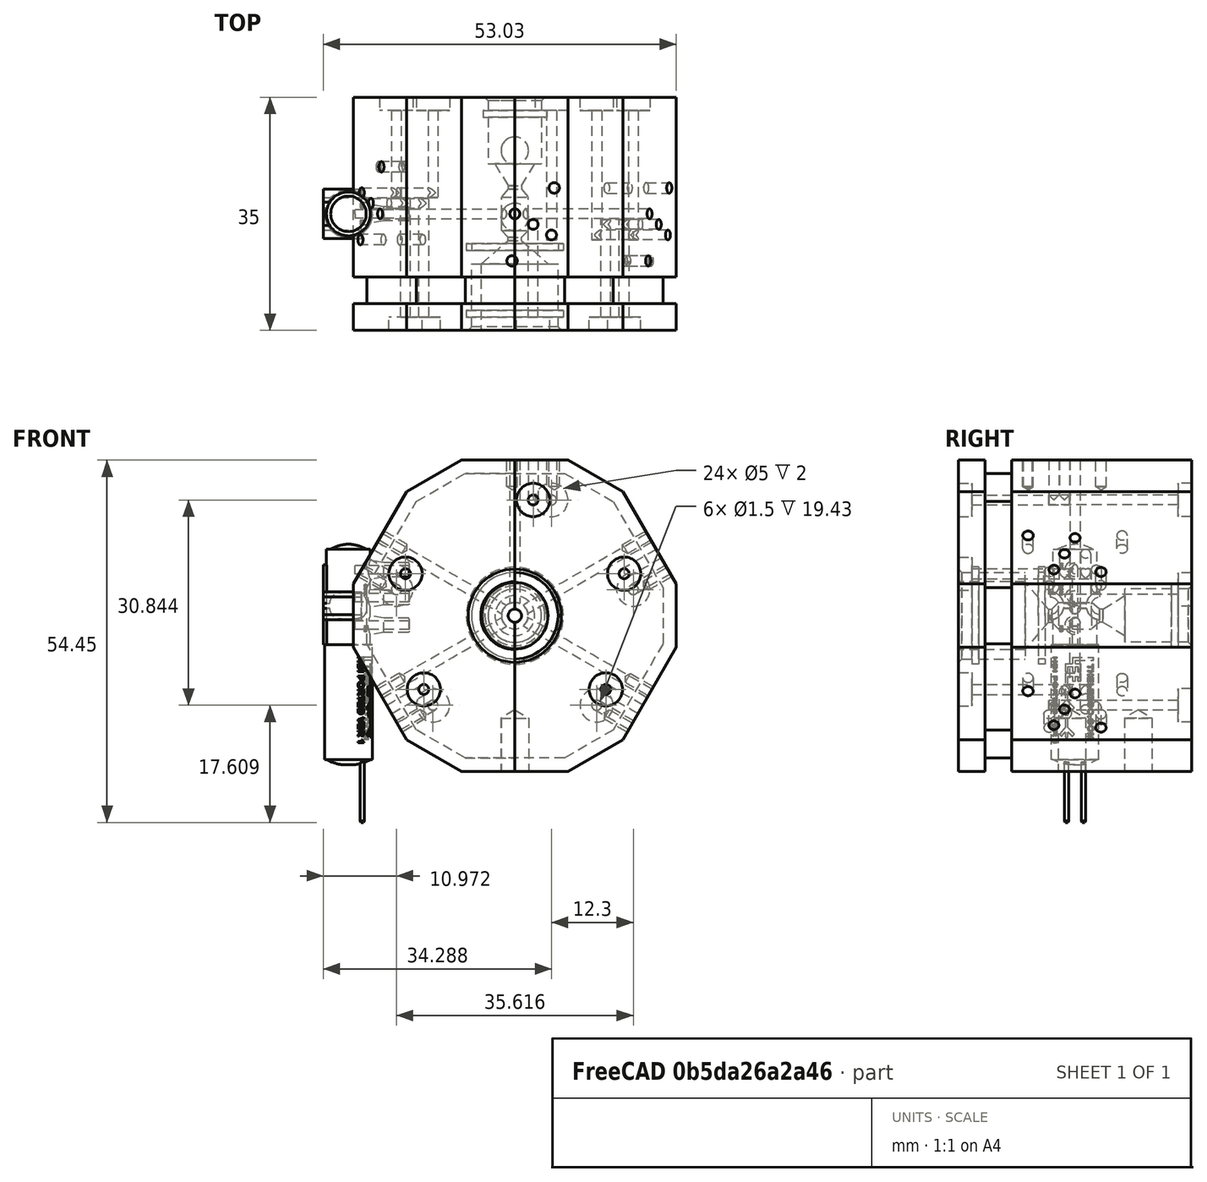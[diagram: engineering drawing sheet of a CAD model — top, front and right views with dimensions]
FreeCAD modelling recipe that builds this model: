
FCSTD DOCUMENT  (FreeCAD 0.18.4R)
Label: main_halved_for_measurements
Comment: # 2020-08-05 14:49:47: read from <userpath>/repositories/sussex_neuro/Olfactometer/hardware/mechanics/from_raiser_et_al/nozzle_big.ipt
License: All rights reserved
LicenseURL: http://en.wikipedia.org/wiki/All_rights_reserved
objects: App::MeasureDistance×10, Part::Feature×6, Part::Cylinder×6, Part::Cut×5, Part::MultiFuse×3, App::FeaturePython×2, Part::Box×2, Part::Fuse×1, PartDesign::FeatureBase×1, PartDesign::Body×1
note: 25 computed .brp shape members not serialized (recipe doc carries the construction recipe); baked Part::Feature solids carry a one-line shape summary decoded from their .brp

FEATURE [Part::Feature] Part__Feature  label="main"
  shape: bbox 48.5 x 35 x 46.77 mm, 148 faces, 0 solids (baked)
FEATURE [Part::Feature] Part__Feature002  label="nozzle_small"
  Placement = pos=(0,2.5,0) rot=(-1,0,0;1.5708rad)
  shape: bbox 8 x 5 x 8 mm, 6 faces (baked)
FEATURE [Part::Feature] Part__Feature004  label="nozzle_big"
  Placement = pos=(0,-2.5,0) rot=(1,0,0;1.5708rad)
  shape: bbox 13 x 5 x 13 mm, 6 faces (baked)
FEATURE [Part::Feature] Part__Feature_solid  label="main (Solid)"
  shape: bbox 48.5 x 35 x 46.77 mm, 148 faces (baked)
FEATURE [Part::MultiFuse] Fusion  label="boddy_fusion_nozzles"
  Shapes = -> [Part__Feature002,Part__Feature004,Part__Feature_solid]
FEATURE [Part::Cylinder] Cylinder
  Angle = 360
  AttacherType = Attacher::AttachEngine3D
  Height = 4
  Placement = pos=(0,2,0) rot=(-1,0,0;1.5708rad)
  Radius = 5
FEATURE [Part::Cylinder] Cylinder001
  Angle = 360
  AttacherType = Attacher::AttachEngine3D
  Height = 11
  Placement = pos=(0,0,0) rot=(-1,0,0;1.5708rad)
  Radius = 4
FEATURE [Part::Fuse] Fusion001
  Base = -> Fusion
FEATURE [Part::Cylinder] Cylinder002
  Angle = 360
  AttacherType = Attacher::AttachEngine3D
  Height = 3
  Placement = pos=(0,-3,0) rot=(1,0,0;1.5708rad)
  Radius = 8
FEATURE [Part::Cylinder] Cylinder003
  Angle = 360
  AttacherType = Attacher::AttachEngine3D
  Height = 11
  Placement = pos=(0,0,0) rot=(1,0,0;1.5708rad)
  Radius = 6
FEATURE [Part::Cut] Cut
  Base = -> Cylinder
  Tool = -> Cylinder001
FEATURE [Part::Cut] Cut001
  Base = -> Cylinder002
  Tool = -> Cylinder003
FEATURE [Part::MultiFuse] Fusion002  label="join_cylinders_to_remove_gap"
  Shapes = -> [Fusion,Cut,Cut001]
FEATURE [PartDesign::FeatureBase] BaseFeature
  BaseFeature = -> Fusion002
FEATURE [PartDesign::Body] Body
  BaseFeature = -> Fusion002
  Group = -> [BaseFeature]
  Origin = -> Origin
  Tip = -> BaseFeature
FEATURE [App::FeaturePython] Dimension  # Draft dimension (typed FeaturePython)
  Diameter = false
  Dimline = (20.9801,-17.5,-0.0116531)
  Direction = (0,0,0)
  Distance = 13.9854
  End = (6.99466,-17.5,-0.0439505)
  Normal = (0,0,-1)
  Start = (-6.99074,-17.5,-0.076248)
FEATURE [App::FeaturePython] Dimension001  # Draft dimension (typed FeaturePython)
  Diameter = false
  Dimline = (19.4569,-16.5402,0.3547)
  Direction = (0,0,0)
  Distance = 12.9618
  End = (6.5,-16.5384,-1e-15)
  Normal = (0,0,1)
  Start = (-6.45693,-16.5366,-0.354704)
FEATURE [Part::Cylinder] Cylinder004
  Angle = 360
  AttacherType = Attacher::AttachEngine3D
  Height = 10
  Placement = pos=(0,0,0) rot=(1,0,0;1.5708rad)
  Radius = 8
FEATURE [Part::Cylinder] Cylinder005
  Angle = 360
  AttacherType = Attacher::AttachEngine3D
  Height = 12
  Placement = pos=(0,1,0) rot=(1,0,0;1.5708rad)
  Radius = 5.1
FEATURE [Part::Cut] Cut002
  Base = -> Cylinder004
  Placement = pos=(0,-7.5,0) rot=(0,0,1;0rad)
  Tool = -> Cylinder005
FEATURE [App::MeasureDistance] Distance  label="Distance: 1.5071 mm"
  Distance = 1.50713
  P1 = (-20.624,0.0157351,11.0435)
  P2 = (-19.8705,0.0259982,12.3487)
FEATURE [Part::Box] Box  label="Cube"
  AttacherType = Attacher::AttachEngine3D
  Height = 50
  Length = 30
  Placement = pos=(0,-25,-25) rot=(0,0,1;0rad)
  Width = 60
FEATURE [Part::MultiFuse] Fusion003  label="join_cylinder_to_fit_glass_tube"
  Shapes = -> [Cut002,Fusion002]
FEATURE [App::MeasureDistance] Distance001  label="Distance: 10.2000 mm"
  Distance = 10.2
  P1 = (-9e-16,-17.5,-5.1)
  P2 = (3e-16,-17.5,5.1)
FEATURE [App::MeasureDistance] Distance002  label="Distance: 2.0226 mm"
  Distance = 2.02263
  P1 = (1e-16,-4,-1)
  P2 = (5e-16,-4.01972,1.02254)
FEATURE [App::MeasureDistance] Distance003  label="Distance: 4.0221 mm"
  Distance = 4.02206
  P1 = (1e-16,2.50363,-1.99702)
  P2 = (0,2.50559,2.02504)
FEATURE [App::MeasureDistance] Distance004  label="Distance: 21.4688 mm"
  Distance = 21.4688
  P1 = (-0.749482,0.00932391,1.91391)
  P2 = (-0.749356,0.005714,23.3827)
FEATURE [App::MeasureDistance] Distance005  label="Distance: 8.0367 mm"
  Distance = 8.03667
  P1 = (2.3e-15,17,-4)
  P2 = (0,16.9738,4.03663)
FEATURE [Part::Box] Box001  label="Cube001"
  AttacherType = Attacher::AttachEngine3D
  Height = 10
  Length = 10
  Placement = pos=(-6,-25.5,-15) rot=(0,0,1;0rad)
  Width = 10
FEATURE [Part::Cut] Cut003
  Base = -> Fusion003
  Tool = -> Box
FEATURE [Part::Feature] obj_0001
  shape: bbox 19.77 x 7.725 x 9.682 mm, 3692 faces, 0 solids (baked)
FEATURE [Part::Cut] Cut004
  Base = -> obj_0001
  Placement = pos=(0,-1.5,0) rot=(0,0,1;0rad)
  Tool = -> Box001
FEATURE [Part::Feature] Part__Feature005  label="LHDA3D00006AA"
  Placement = pos=(-25,0,10) rot=(0,0,1;4.71239rad)
  shape: bbox 12.93 x 7.468 x 41.83 mm, 545 faces (baked)
FEATURE [App::MeasureDistance] Distance006  label="Distance: 0.5000 mm"
  Distance = 0.500014
  P1 = (-0.997332,4.21846,0.0236785)
  P2 = (-0.997758,3.71846,0.0199024)
FEATURE [App::MeasureDistance] Distance007  label="Distance: 1.3771 mm"
  Distance = 1.37711
  P1 = (-1.9697,-2.52642,-0.0344887)
  P2 = (-0.995754,-3.5,-0.0376853)
FEATURE [App::MeasureDistance] Distance008  label="Distance: 5.0029 mm"
  Distance = 5.00293
  P1 = (-1.99707,-2.50293,0)
  P2 = (-2,2.5,0)
FEATURE [App::MeasureDistance] Distance009  label="Distance: 4.0062 mm"
  Distance = 4.00617
  P1 = (0,-1.14791,2)
  P2 = (0,-1.37008,-2)
